# Revit family: P200921MX-038c_MGD5630H_CW
name_source: partatom
category: Specialty Equipment
units: mm (PartAtom-declared; Revit-internal decimal feet)

## family parameters
Always vertical = Yes
Cut with Voids When Loaded = No
Enable Cutting in Views = No
Maintain Annotation Orientation = No
Part Type = Normal
Room Calculation Point = No
Round Connector Dimension = Use Diameter
Shared = No
Work Plane-Based = No

## types (2) — shared parameters
Accent Material = ARCAT - Plastic - Gray
Amps = 0 A
Back Panel Material = ARCAT - Metal - Aluminum
Button Panal Material = ARCAT - Plastic - Dark Grey
Chrome Trim Material = ARCAT - Metal - Chrome
Clearance Material = ARCAT - Clearance
Default Elevation = 0"
Depth = 30 3/4"
Description = Front Load Gas Dryer with Extra Power and Quick Dry cycle - 7.3 cu. ft.
Sécheuse au gaz avec fonction Extra Power, 7.3 pi³
Dimension Guide = http://whirlpool.com
http://whirlpool.com
Display Material = ARCAT - Plastic - White
Door Material = ARCAT - Metal - Steel - Gray
Dsiplay Panel Material = ARCAT - Glass Tempered - Black
Family Name = Laundry
Feature 1 = Extra Power Button
Bouton d’amplification de puissance Extra Power
Feature 2 = Advanced Moisture Sensing
Détection d'humidité perfectionnée
Feature 3 = Quick Dry Cycle
Programme de séchage rapide
Glass Material = ARCAT - Glass Tempered - Clear
Handle Material = ARCAT - Plastic, ABS - Black
Height = 38 3/4"
Installation-Fabrication = https://www.whirlpool.com
https://www.whirlpool.com
Knob Material = ARCAT - Plastic - Gray Light
Leg Material = ARCAT - Plastic - White
Manufacturer = Maytag
Voltage = 0 V
Width = 27"

## per-type parameters (varying)
| type | Body Material |
| MGD5630HC | ARCAT - Metal - Steel - Gray |
| MGD5630HW | ARCAT - Metal - Steel - White |

note: column(s) folded — value = type name in every type: Model

## geometry (parser evidence)
native form markers: Sweep x8
no freeform markers — native parametric forms only
